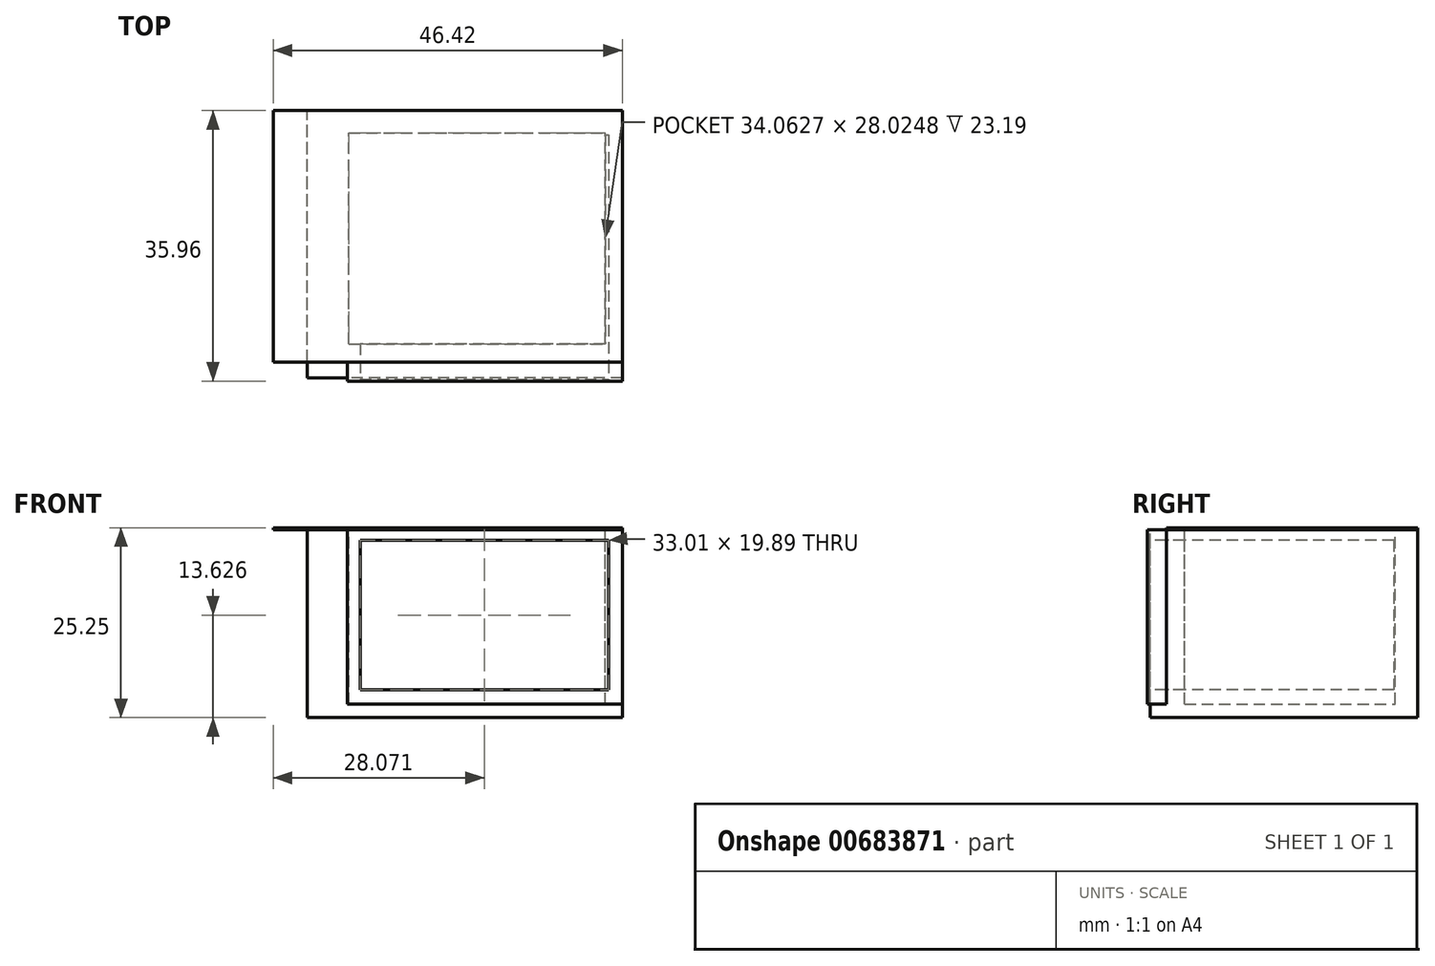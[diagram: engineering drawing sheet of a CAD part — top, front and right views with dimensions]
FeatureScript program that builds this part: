
annotation { "Feature Type Name" : "Feature", "Feature Type Description" : "" }
export const myFeature = defineFeature(function(context is Context, id is Id, definition is map)
    precondition{}
    {
        {
            var Q0;
            Q0=qCreatedBy(makeId("Front.planeOp"),FACE);
            var sketch = newSketch(context, id + "F0", { "sketchPlane" : qUnion([Q0])});
            skLineSegment(sketch, "E0.bottom", {"start": v(20.95, -12.5) * mm, "end": v(-20.95, -12.5) * mm});
            skLineSegment(sketch, "E0.top", {"start": v(20.95, 12.5) * mm, "end": v(-20.95, 12.5) * mm});
            skLineSegment(sketch, "E0.left", {"start": v(20.95, -12.5) * mm, "end": v(20.95, 12.5) * mm});
            skLineSegment(sketch, "E0.right", {"start": v(-20.95, -12.5) * mm, "end": v(-20.95, 12.5) * mm});
            skPoint(sketch, "E0.middle", {"position": v(0, 0) * mm});
            skSolve(sketch);
        }
        {
            var Q0;
            Q0 = qSketchRegion(id + "F0", true);
            extrude(context, id + "F1", {"entities" : qUnion([Q0]), "depth" : 17.78 * mm, "offsetDistance" : 25.4 * mm, "hasSecondDirection" : true, "secondDirectionOppositeDirection" : true, "secondDirectionDepth" : 17.78 * mm});
        }
        {
            var Q0;
            Q0=makeQuery(id+"F1.opExtrude","SWEPT_FACE",FACE,{"disambiguationData":[OSD([sQuery(id+"F0.wireOp",EDGE,"E0.top")])]});
            var sketch = newSketch(context, id + "F2", { "sketchPlane" : qUnion([Q0])});
            skLineSegment(sketch, "E1.bottom", {"start": v(20.95, -17.78) * mm, "end": v(-15.6, -17.78) * mm});
            skLineSegment(sketch, "E1.top", {"start": v(20.95, -15.64) * mm, "end": v(-15.6, -15.64) * mm});
            skLineSegment(sketch, "E1.left", {"start": v(20.95, -17.78) * mm, "end": v(20.95, -15.64) * mm});
            skLineSegment(sketch, "E1.right", {"start": v(-15.6, -17.78) * mm, "end": v(-15.6, -15.64) * mm});
            skSolve(sketch);
        }
        {
            var Q0;
            Q0 = qSketchRegion(id + "F2", true);
            extrude(context, id + "F3", {"entities" : qUnion([Q0]), "operationType" : NewBodyOperationType.REMOVE, "oppositeDirection" : true, "depth" : 23.2 * mm, "offsetDistance" : 25.4 * mm});
        }
        {
            var Q0;
            Q0=makeQuery(id+"F3.boolean.opBoolean","COPY",FACE,{"derivedFrom":makeQuery(id+"F3.opExtrude","SWEPT_FACE",FACE,{"disambiguationData":[OSD([sQuery(id+"F2.wireOp",EDGE,"E1.top")])]})});
            var sketch = newSketch(context, id + "F4", { "sketchPlane" : qUnion([Q0])});
            skLineSegment(sketch, "E2.bottom", {"start": v(-15.6, 12.5) * mm, "end": v(20.95, 12.5) * mm});
            skLineSegment(sketch, "E2.top", {"start": v(-15.6, -10.7) * mm, "end": v(20.95, -10.7) * mm});
            skLineSegment(sketch, "E2.left", {"start": v(-15.6, 12.5) * mm, "end": v(-15.6, -10.7) * mm});
            skLineSegment(sketch, "E2.right", {"start": v(20.95, 12.5) * mm, "end": v(20.95, -10.7) * mm});
            skSolve(sketch);
        }
        {
            var Q0;
            Q0 = qSketchRegion(id + "F4", true);
            extrude(context, id + "F5", {"entities" : qUnion([Q0]), "depth" : 2.54 * mm, "offsetDistance" : 25.4 * mm});
        }
        {
            var Q0;
            Q0=makeQuery(id+"F5.opExtrude","CAP_FACE",FACE,{"disambiguationData":[OSD([sQuery(id+"F4.wireOp",EDGE,"E2.bottom"),sQuery(id+"F4.wireOp",EDGE,"E2.top"),sQuery(id+"F4.wireOp",EDGE,"E2.left"),sQuery(id+"F4.wireOp",EDGE,"E2.right")])],"isStart":false});
            var sketch = newSketch(context, id + "F6", { "sketchPlane" : qUnion([Q0])});
            skLineSegment(sketch, "E3.bottom", {"start": v(-13.9, 11.07) * mm, "end": v(19.1, 11.07) * mm});
            skLineSegment(sketch, "E3.top", {"start": v(-13.9, -8.82) * mm, "end": v(19.1, -8.82) * mm});
            skLineSegment(sketch, "E3.left", {"start": v(-13.9, 11.07) * mm, "end": v(-13.9, -8.82) * mm});
            skLineSegment(sketch, "E3.right", {"start": v(19.1, 11.07) * mm, "end": v(19.1, -8.82) * mm});
            skSolve(sketch);
        }
        {
            var Q0;
            Q0 = qSketchRegion(id + "F6", true);
            extrude(context, id + "F7", {"entities" : qUnion([Q0]), "operationType" : NewBodyOperationType.REMOVE, "oppositeDirection" : true, "depth" : 32.77 * mm, "offsetDistance" : 25.4 * mm});
        }
        {
            var Q0;
            Q0=makeQuery(id+"F5.opExtrude","CAP_FACE",FACE,{"disambiguationData":[OSD([sQuery(id+"F4.wireOp",EDGE,"E2.bottom"),sQuery(id+"F4.wireOp",EDGE,"E2.top"),sQuery(id+"F4.wireOp",EDGE,"E2.left"),sQuery(id+"F4.wireOp",EDGE,"E2.right")])],"isStart":false});
            var sketch = newSketch(context, id + "F8", { "sketchPlane" : qUnion([Q0])});
            skLineSegment(sketch, "E4.bottom", {"start": v(-13.9, 11.07) * mm, "end": v(19.1, 11.07) * mm});
            skLineSegment(sketch, "E4.top", {"start": v(-13.9, -8.82) * mm, "end": v(19.1, -8.82) * mm});
            skLineSegment(sketch, "E4.left", {"start": v(-13.9, 11.07) * mm, "end": v(-13.9, -8.82) * mm});
            skLineSegment(sketch, "E4.right", {"start": v(19.1, 11.07) * mm, "end": v(19.1, -8.82) * mm});
            skSolve(sketch);
        }
        {
            var Q0;
            Q0 = qSketchRegion(id + "F8", true);
            extrude(context, id + "F9", {"entities" : qUnion([Q0]), "oppositeDirection" : true, "depth" : 0.25 * mm, "offsetDistance" : 25.4 * mm});
        }
        {
            var Q0;
            Q0=makeQuery(id+"F1.opExtrude","SWEPT_FACE",FACE,{"disambiguationData":[OSD([sQuery(id+"F0.wireOp",EDGE,"E0.top")])]});
            var sketch = newSketch(context, id + "F10", { "sketchPlane" : qUnion([Q0])});
            skLineSegment(sketch, "E5.bottom", {"start": v(-15.39, -13.22) * mm, "end": v(18.68, -13.22) * mm});
            skLineSegment(sketch, "E5.top", {"start": v(-15.39, 14.8) * mm, "end": v(18.68, 14.8) * mm});
            skLineSegment(sketch, "E5.left", {"start": v(-15.39, -13.22) * mm, "end": v(-15.39, 14.8) * mm});
            skLineSegment(sketch, "E5.right", {"start": v(18.68, -13.22) * mm, "end": v(18.68, 14.8) * mm});
            skSolve(sketch);
        }
        {
            var Q0;
            Q0 = qSketchRegion(id + "F10", true);
            extrude(context, id + "F11", {"entities" : qUnion([Q0]), "operationType" : NewBodyOperationType.REMOVE, "oppositeDirection" : true, "depth" : 23.2 * mm, "offsetDistance" : 25.4 * mm});
        }
        {
            var Q0;
            Q0=makeQuery(id+"F1.opExtrude","SWEPT_FACE",FACE,{"disambiguationData":[OSD([sQuery(id+"F0.wireOp",EDGE,"E0.top")])]});
            var sketch = newSketch(context, id + "F12", { "sketchPlane" : qUnion([Q0])});
            skLineSegment(sketch, "E6.bottom", {"start": v(20.95, 17.78) * mm, "end": v(-25.47, 17.78) * mm});
            skLineSegment(sketch, "E6.top", {"start": v(20.95, -15.64) * mm, "end": v(-25.47, -15.64) * mm});
            skLineSegment(sketch, "E6.left", {"start": v(20.95, 17.78) * mm, "end": v(20.95, -15.64) * mm});
            skLineSegment(sketch, "E6.right", {"start": v(-25.47, 17.78) * mm, "end": v(-25.47, -15.64) * mm});
            skSolve(sketch);
        }
        {
            var Q0;
            Q0 = qSketchRegion(id + "F12", true);
            extrude(context, id + "F13", {"entities" : qUnion([Q0]), "depth" : 0.25 * mm, "offsetDistance" : 25.4 * mm});
        }
    });
